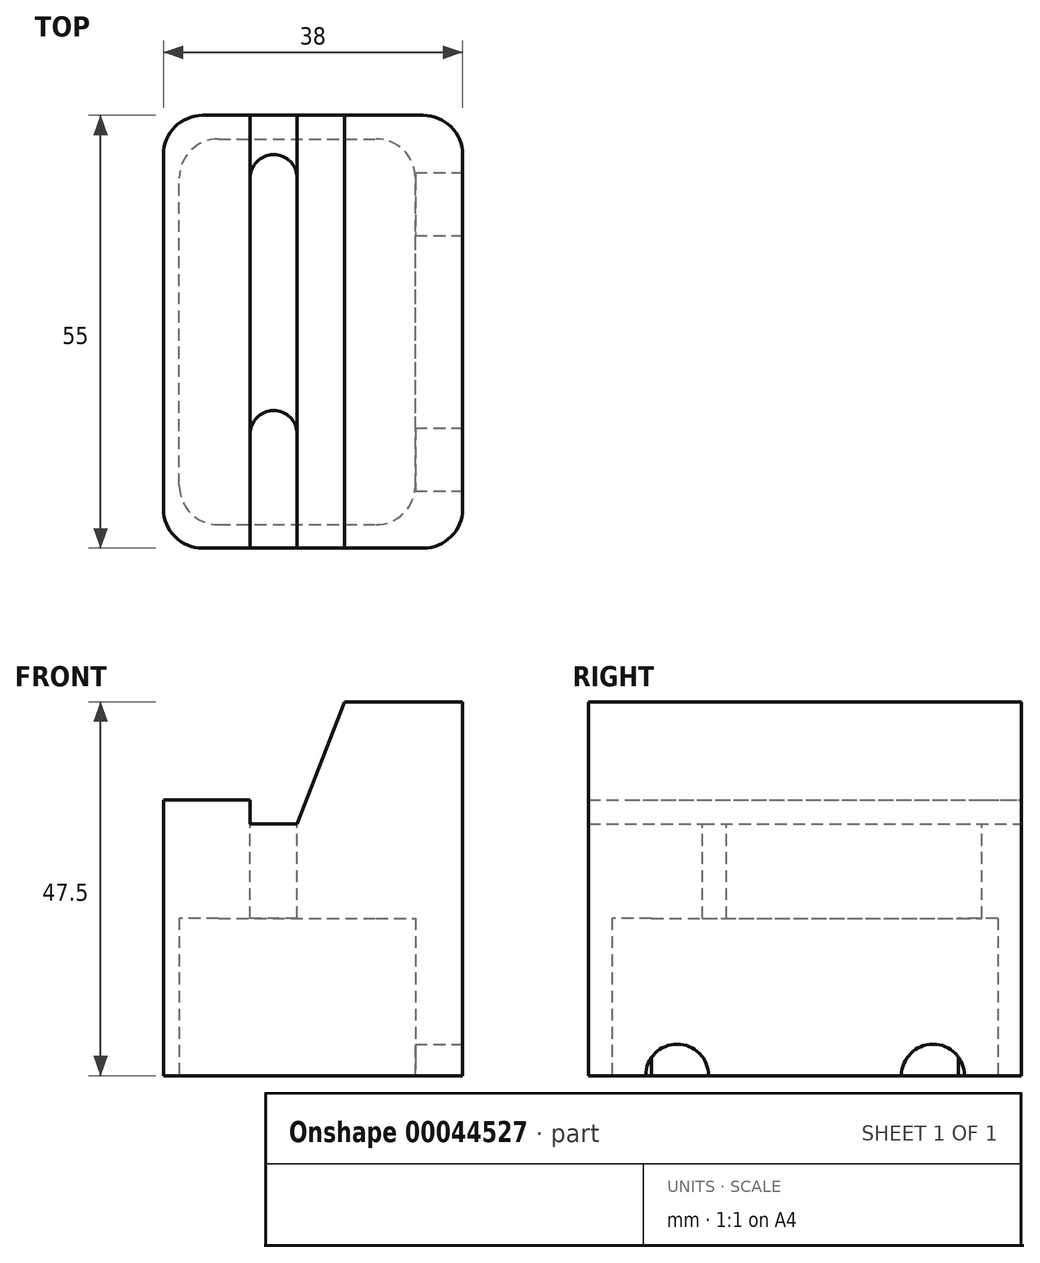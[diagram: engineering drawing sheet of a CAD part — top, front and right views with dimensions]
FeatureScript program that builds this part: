
annotation { "Feature Type Name" : "Feature", "Feature Type Description" : "" }
export const myFeature = defineFeature(function(context is Context, id is Id, definition is map)
    precondition{}
    {
        {
            var Q0;
            Q0=qCreatedBy(makeId("Front.planeOp"),FACE);
            var sketch = newSketch(context, id + "F0", { "sketchPlane" : qUnion([Q0])});
            skLineSegment(sketch, "E0", {"start": v(0, 0) * mm, "end": v(38, 0) * mm});
            skLineSegment(sketch, "E1", {"start": v(38, 0) * mm, "end": v(38, 47.5) * mm});
            skLineSegment(sketch, "E2", {"start": v(38, 47.5) * mm, "end": v(23, 47.5) * mm});
            skLineSegment(sketch, "E3", {"start": v(23, 47.5) * mm, "end": v(17, 32) * mm});
            skLineSegment(sketch, "E4", {"start": v(17, 32) * mm, "end": v(11, 32) * mm});
            skLineSegment(sketch, "E5", {"start": v(11, 32) * mm, "end": v(11, 35) * mm});
            skLineSegment(sketch, "E6", {"start": v(11, 35) * mm, "end": v(0, 35) * mm});
            skLineSegment(sketch, "E7", {"start": v(0, 35) * mm, "end": v(0, 0) * mm});
            skSolve(sketch);
        }
        {
            var Q0;
            Q0=makeQuery(id+"F0.imprint","IMPRINT",FACE,{"disambiguationData":[TD([[makeQuery(id+"F0.imprint","IMPRINT",EDGE,{"derivedFrom":sQuery(id+"F0.wireOp",EDGE,"E0")}),1.0]])]});
            var Q1;
            Q1 = qSketchRegion(id + "F2", true);
            extrude(context, id + "F1", {"entities" : qUnion([Q0, Q1]), "depth" : 55 * mm});
        }
        {
            var Q0;
            Q0=makeQuery(id+"F1.opExtrude","SWEPT_FACE",FACE,{"disambiguationData":[OSD([sQuery(id+"F0.wireOp",EDGE,"E4")])]});
            var sketch = newSketch(context, id + "F2", { "sketchPlane" : qUnion([Q0])});
            skLineSegment(sketch, "E8.bottom", {"start": v(14, -5) * mm, "end": v(14, -5) * mm});
            skLineSegment(sketch, "E8.top", {"start": v(14, -17.5) * mm, "end": v(14, -17.5) * mm});
            skLineSegment(sketch, "E8.left", {"start": v(11, -8) * mm, "end": v(11, -14.5) * mm});
            skLineSegment(sketch, "E8.right", {"start": v(17, -8) * mm, "end": v(17, -14.5) * mm});
            skPoint(sketch, "E9.visualSharp", {"position": v(17, -5) * mm});
            skArc(sketch, "E9.filletArc", {"start": v(17, -8) * mm, "mid": v(16.12, -5.88) * mm, "end": v(14, -5) * mm});
            skPoint(sketch, "E10.visualSharp", {"position": v(17, -17.5) * mm});
            skArc(sketch, "E10.filletArc", {"start": v(14, -17.5) * mm, "mid": v(16.12, -16.62) * mm, "end": v(17, -14.5) * mm});
            skPoint(sketch, "E11.visualSharp", {"position": v(11, -17.5) * mm});
            skArc(sketch, "E11.filletArc", {"start": v(11, -14.5) * mm, "mid": v(11.88, -16.62) * mm, "end": v(14, -17.5) * mm});
            skPoint(sketch, "E12.visualSharp", {"position": v(11, -5) * mm});
            skArc(sketch, "E12.filletArc", {"start": v(14, -5) * mm, "mid": v(11.88, -5.88) * mm, "end": v(11, -8) * mm});
            skLineSegment(sketch, "E13", {"start": v(57.35, -27.5) * mm, "end": v(-24.53, -27.5) * mm, "construction": true});
            skArc(sketch, "E14.MirrorCS", {"start": v(11, -40.5) * mm, "mid": v(11.88, -38.38) * mm, "end": v(14, -37.5) * mm});
            skArc(sketch, "E15.MirrorCS", {"start": v(14, -37.5) * mm, "mid": v(16.12, -38.38) * mm, "end": v(17, -40.5) * mm});
            skLineSegment(sketch, "E16.MirrorCS", {"start": v(17, -47) * mm, "end": v(17, -40.5) * mm});
            skArc(sketch, "E17.MirrorCS", {"start": v(17, -47) * mm, "mid": v(16.12, -49.12) * mm, "end": v(14, -50) * mm});
            skArc(sketch, "E18.MirrorCS", {"start": v(14, -50) * mm, "mid": v(11.88, -49.12) * mm, "end": v(11, -47) * mm});
            skLineSegment(sketch, "E19.MirrorCS", {"start": v(11, -47) * mm, "end": v(11, -40.5) * mm});
            skLineSegment(sketch, "E20.0", {"start": v(5, -5) * mm, "end": v(33, -5) * mm});
            skLineSegment(sketch, "E20.1", {"start": v(5, -50) * mm, "end": v(5, -5) * mm});
            skLineSegment(sketch, "E20.2", {"start": v(33, -50) * mm, "end": v(5, -50) * mm});
            skLineSegment(sketch, "E20.3", {"start": v(33, -5) * mm, "end": v(33, -50) * mm});
            skSolve(sketch);
        }
        {
            var Q0;
            Q0=makeQuery(id+"F2.imprint","IMPRINT",FACE,{"disambiguationData":[TD([[makeQuery(id+"F2.imprint","IMPRINT",EDGE,{"derivedFrom":sQuery(id+"F2.wireOp",EDGE,"E8.left")}),-1.0]])]});
            var Q1;
            Q1=makeQuery(id+"F2.imprint","IMPRINT",FACE,{"disambiguationData":[TD([[makeQuery(id+"F2.imprint","IMPRINT",EDGE,{"derivedFrom":sQuery(id+"F2.wireOp",EDGE,"E14.MirrorCS")}),-1.0]])]});
            extrude(context, id + "F3", {"entities" : qUnion([Q0, Q1]), "operationType" : NewBodyOperationType.REMOVE, "endBound" : BoundingType.THROUGH_ALL, "oppositeDirection" : true, "depth" : 15 * mm});
        }
        {
            var Q0;
            Q0=makeQuery(id+"F1.opExtrude","CAP_EDGE",EDGE,{"disambiguationData":[OSD([sQuery(id+"F0.wireOp",EDGE,"E1")])],"isStart":false});
            var Q1;
            Q1=makeQuery(id+"F1.opExtrude","CAP_EDGE",EDGE,{"disambiguationData":[OSD([sQuery(id+"F0.wireOp",EDGE,"E1")])],"isStart":true});
            fillet(context, id + "F4", {"entities" : qUnion([Q0, Q1]), "radius" : 5 * mm, "tangentPropagation" : true, "allowEdgeOverflow" : false});
        }
        {
            var Q0;
            Q0=makeQuery(id+"F1.opExtrude","CAP_EDGE",EDGE,{"disambiguationData":[OSD([sQuery(id+"F0.wireOp",EDGE,"E7")])],"isStart":true});
            var Q1;
            Q1=makeQuery(id+"F1.opExtrude","CAP_EDGE",EDGE,{"disambiguationData":[OSD([sQuery(id+"F0.wireOp",EDGE,"E7")])],"isStart":false});
            fillet(context, id + "F5", {"entities" : qUnion([Q0, Q1]), "radius" : 5 * mm, "tangentPropagation" : true, "allowEdgeOverflow" : false});
        }
        {
            var Q0;
            Q0=makeQuery(id+"F1.opExtrude","SWEPT_FACE",FACE,{"disambiguationData":[OSD([sQuery(id+"F0.wireOp",EDGE,"E0")])]});
            var sketch = newSketch(context, id + "F6", { "sketchPlane" : qUnion([Q0])});
            skLineSegment(sketch, "E21.bottom", {"start": v(7, 52) * mm, "end": v(27, 52) * mm});
            skLineSegment(sketch, "E21.top", {"start": v(7, 3) * mm, "end": v(27, 3) * mm});
            skLineSegment(sketch, "E21.left", {"start": v(2, 47) * mm, "end": v(2, 8) * mm});
            skLineSegment(sketch, "E21.right", {"start": v(32, 47) * mm, "end": v(32, 8) * mm});
            skPoint(sketch, "E22.visualSharp", {"position": v(32, 52) * mm});
            skArc(sketch, "E22.filletArc", {"start": v(32, 47) * mm, "mid": v(30.54, 50.54) * mm, "end": v(27, 52) * mm});
            skPoint(sketch, "E23.visualSharp", {"position": v(32, 3) * mm});
            skArc(sketch, "E23.filletArc", {"start": v(27, 3) * mm, "mid": v(30.54, 4.46) * mm, "end": v(32, 8) * mm});
            skPoint(sketch, "E24.visualSharp", {"position": v(2, 3) * mm});
            skArc(sketch, "E24.filletArc", {"start": v(2, 8) * mm, "mid": v(3.46, 4.46) * mm, "end": v(7, 3) * mm});
            skPoint(sketch, "E25.visualSharp", {"position": v(2, 52) * mm});
            skArc(sketch, "E25.filletArc", {"start": v(7, 52) * mm, "mid": v(3.46, 50.54) * mm, "end": v(2, 47) * mm});
            skSolve(sketch);
        }
        {
            var Q0;
            Q0=makeQuery(id+"F6.imprint","IMPRINT",FACE,{"disambiguationData":[TD([[makeQuery(id+"F6.imprint","IMPRINT",EDGE,{"derivedFrom":sQuery(id+"F6.wireOp",EDGE,"E21.bottom")}),-1.0]])]});
            extrude(context, id + "F7", {"entities" : qUnion([Q0]), "operationType" : NewBodyOperationType.REMOVE, "oppositeDirection" : true, "depth" : 20 * mm});
        }
        {
            var Q0;
            Q0=makeQuery(id+"F1.opExtrude","SWEPT_FACE",FACE,{"disambiguationData":[OSD([sQuery(id+"F0.wireOp",EDGE,"E1")])]});
            var sketch = newSketch(context, id + "F8", { "sketchPlane" : qUnion([Q0])});
            skCircle(sketch, "E26", {"center": v(-43.75, 0) * mm, "radius": 4 * mm});
            skCircle(sketch, "E27", {"center": v(-11.25, 0) * mm, "radius": 4 * mm});
            skSolve(sketch);
        }
        {
            var Q0;
            {var subQ0=sQuery(id+"F8.wireOp",EDGE,"E26");var subQ1=makeQuery(id+"F1.opExtrude","SWEPT_EDGE",EDGE,{"disambiguationData":[OSD([sQuery(id+"F0.wireOp",EDGE,"E0"),sQuery(id+"F0.wireOp",EDGE,"E1")])]});var subQ2=makeQuery(id+"F8.imprint","INTERSECT",VERTEX,{"disambiguationData":[OD(0.0)],"derivedFrom":[subQ1,subQ0]});Q0=makeQuery(id+"F8.imprint","IMPRINT",FACE,{"disambiguationData":[TD([[makeQuery(id+"F8.imprint","IMPRINT",EDGE,{"disambiguationData":[TD([[subQ2,1.0]])],"derivedFrom":subQ0}),1.0]])]});}
            var Q1;
            {var subQ0=sQuery(id+"F8.wireOp",EDGE,"E27");var subQ1=makeQuery(id+"F1.opExtrude","SWEPT_EDGE",EDGE,{"disambiguationData":[OSD([sQuery(id+"F0.wireOp",EDGE,"E0"),sQuery(id+"F0.wireOp",EDGE,"E1")])]});var subQ2=makeQuery(id+"F8.imprint","INTERSECT",VERTEX,{"disambiguationData":[OD(0.0)],"derivedFrom":[subQ1,subQ0]});Q1=makeQuery(id+"F8.imprint","IMPRINT",FACE,{"disambiguationData":[TD([[makeQuery(id+"F8.imprint","IMPRINT",EDGE,{"disambiguationData":[TD([[subQ2,-1.0]])],"derivedFrom":subQ0}),1.0]])]});}
            extrude(context, id + "F9", {"entities" : qUnion([Q0, Q1]), "operationType" : NewBodyOperationType.REMOVE, "oppositeDirection" : true, "depth" : 6 * mm});
        }
    });
